# Revit family: Квайтлайн_Eng
name_source: partatom
category: Mechanical Equipment
units: mm (PartAtom-declared; Revit-internal decimal feet)

## family parameters
Always vertical = Yes
Classification = None
Cut with Voids When Loaded = No
Part Type = Normal
Room Calculation Point = No
Round Connector Dimension = Use Diameter
Shared = No
Work Plane-Based = No

## types (6) — shared parameters
00_20_Manufacturer = Vents
00_20_Name = Axial inline fan
Amperage = 0 A
Casing Material = Plastic, opaque, white
Frequency = 50 Hz
Load Classification = HVAC
Maintenance zone material = <By Category>
Manufacturer = Vents
Number of Fase = 1
URL = https://ventilation-system.com
Voltage = 230 V
zero-valued in all types: Default Elevation

## per-type parameters (varying)
| type | B | D | Diameter | Dy | Frame | Frame_K | H | Height | L | Length | Maximum Air Flow | Power | R | Ry | Sound pressure level at 3 m distance | Weight | Width |
| Quietline 100 | 160 mm  [stored 0.524934 ft] | 100 mm  [stored 0.328084 ft] | 100 mm  [stored 0.328084 ft] | 98 mm  [stored 0.321522 ft] | Frame : 100 | No | 114 mm  [stored 0.374016 ft] | 114 mm  [stored 0.374016 ft] | 138 mm  [stored 0.452756 ft] | 138 mm  [stored 0.452756 ft] | 100.0 m³/h | 8 W | 50 mm  [stored 0.164042 ft] | 49 mm  [stored 0.160761 ft] | 25 dBA | 0.61 kg | 160 mm  [stored 0.524934 ft] |
| Quietline 125 | 185 mm  [stored 0.606955 ft] | 125 mm  [stored 0.410105 ft] | 125 mm  [stored 0.410105 ft] | 123 mm  [stored 0.403543 ft] | Frame : 125 | No | 139 mm  [stored 0.456037 ft] | 139 mm  [stored 0.456037 ft] | 162 mm | 162 mm | 197.0 m³/h | 13 W | 63 mm | 62 mm | 32 | 0.75 kg | 185 mm  [stored 0.606955 ft] |
| Quietline 150 | 200 mm  [stored 0.656168 ft] | 150 mm | 150 mm | 148 mm  [stored 0.485564 ft] | Frame : 150 | No | 163 mm  [stored 0.534777 ft] | 163 mm  [stored 0.534777 ft] | 182 mm  [stored 0.597113 ft] | 182 mm  [stored 0.597113 ft] | 335.0 m³/h | 22 W | 75 mm | 74 mm  [stored 0.242782 ft] | 39 dBA | 1.30 kg | 200 mm  [stored 0.656168 ft] |
| Quietline-k 100 | 160 mm  [stored 0.524934 ft] | 100 mm  [stored 0.328084 ft] | 100 mm  [stored 0.328084 ft] | 98 mm  [stored 0.321522 ft] | Frame : 100 | Yes | 114 mm  [stored 0.374016 ft] | 114 mm  [stored 0.374016 ft] | 138 mm  [stored 0.452756 ft] | 138 mm  [stored 0.452756 ft] | 100.0 m³/h | 8 W | 50 mm  [stored 0.164042 ft] | 49 mm  [stored 0.160761 ft] | 25 dBA | 0.61 kg | 160 mm  [stored 0.524934 ft] |
| Quietline-k 150 | 200 mm  [stored 0.656168 ft] | 150 mm | 150 mm | 148 mm  [stored 0.485564 ft] | Frame : 150 | Yes | 163 mm  [stored 0.534777 ft] | 163 mm  [stored 0.534777 ft] | 182 mm  [stored 0.597113 ft] | 182 mm  [stored 0.597113 ft] | 335.0 m³/h | 22 W | 75 mm | 74 mm  [stored 0.242782 ft] | 39 dBA | 1.30 kg | 200 mm  [stored 0.656168 ft] |
| Quietline-k 125 | 185 mm  [stored 0.606955 ft] | 125 mm  [stored 0.410105 ft] | 125 mm  [stored 0.410105 ft] | 123 mm  [stored 0.403543 ft] | Frame : 125 | Yes | 139 mm  [stored 0.456037 ft] | 139 mm  [stored 0.456037 ft] | 162 mm | 162 mm | 197.0 m³/h | 13 W | 63 mm | 62 mm | 32 dBA | 0.75 kg | 185 mm  [stored 0.606955 ft] |

note: column(s) folded — value = type name in every type: 00_20_Type

note: [stored X ft] marks values corroborated as IEEE doubles in the binary element streams (Revit-internal decimal feet)
